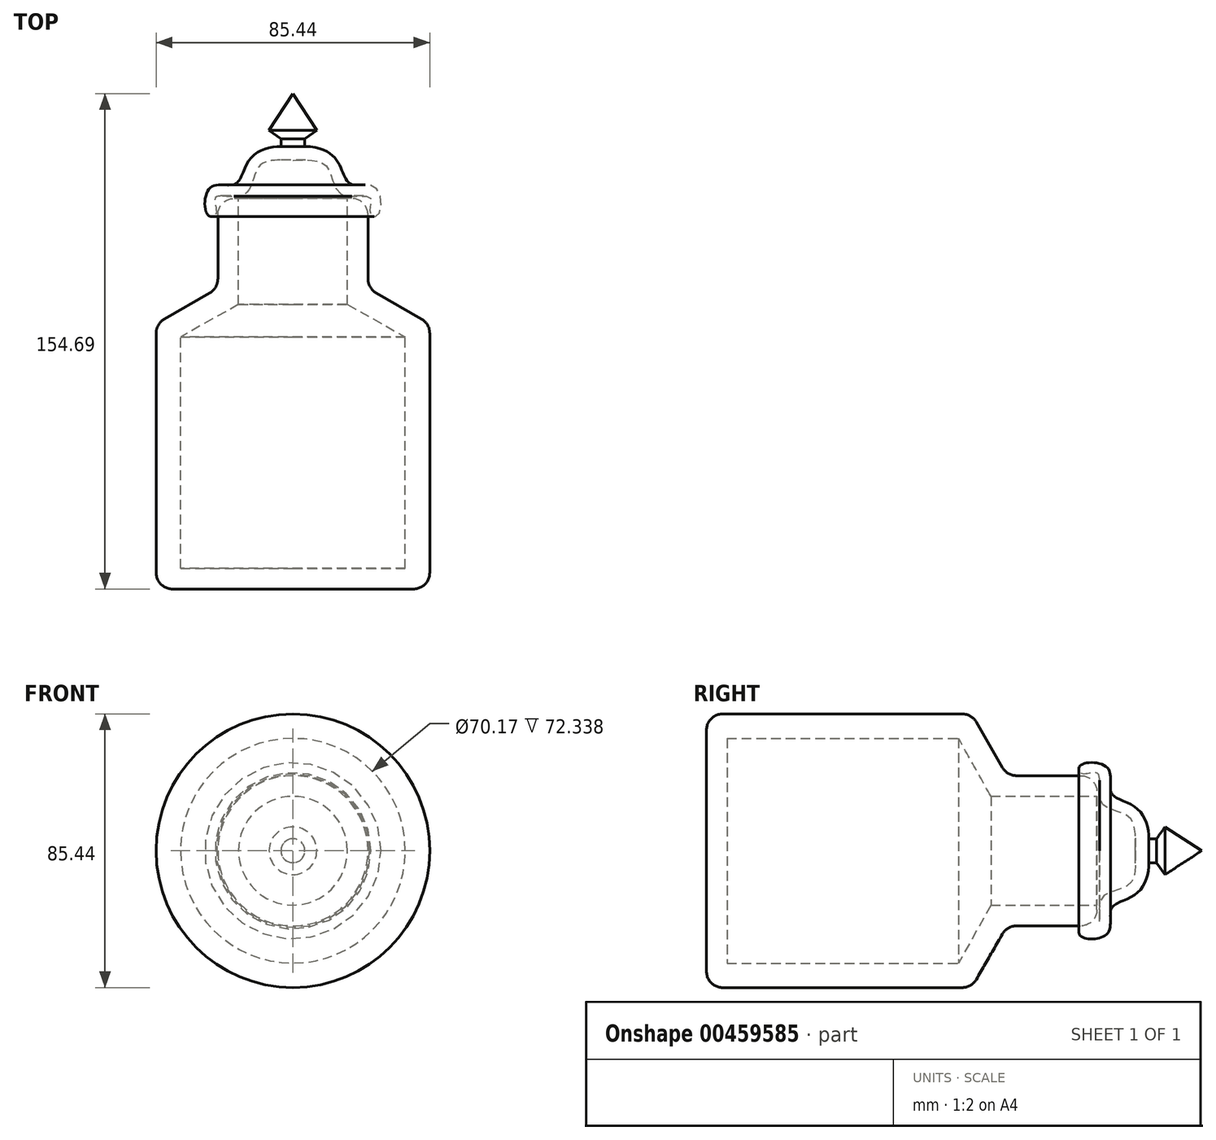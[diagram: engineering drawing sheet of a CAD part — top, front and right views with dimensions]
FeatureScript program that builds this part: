
annotation { "Feature Type Name" : "Feature", "Feature Type Description" : "" }
export const myFeature = defineFeature(function(context is Context, id is Id, definition is map)
    precondition{}
    {
        {
            var Q0;
            Q0=qCreatedBy(makeId("Top.planeOp"),FACE);
            var sketch = newSketch(context, id + "F0", { "sketchPlane" : qUnion([Q0])});
            skLineSegment(sketch, "E0", {"start": v(0, 75.39) * mm, "end": v(0, -75.47) * mm});
            skLineSegment(sketch, "E1", {"start": v(0, -64.48) * mm, "end": v(42.72, -64.48) * mm});
            skLineSegment(sketch, "E2", {"start": v(42.72, -64.48) * mm, "end": v(42.72, 18.34) * mm});
            skLineSegment(sketch, "E3", {"start": v(42.72, 18.34) * mm, "end": v(23.45, 29.44) * mm});
            skLineSegment(sketch, "E4", {"start": v(23.45, 29.44) * mm, "end": v(23.45, 57.48) * mm});
            skLineSegment(sketch, "E5", {"start": v(23.45, 57.48) * mm, "end": v(16.99, 57.48) * mm});
            skLineSegment(sketch, "E6", {"start": v(16.99, 57.48) * mm, "end": v(16.99, 24.36) * mm});
            skLineSegment(sketch, "E7", {"start": v(16.99, 24.36) * mm, "end": v(35.09, 14.27) * mm});
            skLineSegment(sketch, "E8", {"start": v(35.09, 14.27) * mm, "end": v(35.09, -58.07) * mm});
            skLineSegment(sketch, "E9", {"start": v(35.09, -58.07) * mm, "end": v(0, -58.07) * mm});
            skLineSegment(sketch, "E10", {"start": v(0, 75.39) * mm, "end": v(0, 95.93) * mm});
            skFitSpline(sketch, "E11", {"points": [v(0, 69.4) * mm, v(10.5, 67.6) * mm, v(15.16, 58.75) * mm, v(24.12, 57.75) * mm, v(24.06, 52.73) * mm, v(26.53, 52.26) * mm, v(25.73, 60.9) * mm, v(17.61, 62.26) * mm, v(3.72, 73.7) * mm], "startDerivative": vector(90.25, 0.02) * mm, "endDerivative": vector(-199.47, 2.25) * mm});
            skLineSegment(sketch, "E12", {"start": v(7.45, 78.77) * mm, "end": v(0, 90.21) * mm});
            skPoint(sketch, "E13.end.orphan", {"position": v(3.72, 78.77) * mm});
            skLineSegment(sketch, "E14", {"start": v(3.72, 73.7) * mm, "end": v(3.72, 76.1) * mm});
            skLineSegment(sketch, "E15", {"start": v(7.45, 78.77) * mm, "end": v(3.72, 76.1) * mm});
            skSolve(sketch);
        }
        {
            var Q0;
            Q0 = qSketchRegion(id + "F0", true);
            var Q1;
            Q1=sQuery(id+"F0.wireOp",EDGE,"E0");
            revolve(context, id + "F1", {"entities" : qUnion([Q0]), "axis" : qUnion([Q1]), "revolveType" : RevolveType.FULL});
        }
        {
            var Q0;
            Q0=makeQuery(id+"F1.opRevolve","SWEPT_EDGE",EDGE,{"disambiguationData":[OSD([sQuery(id+"F0.wireOp",EDGE,"E2"),sQuery(id+"F0.wireOp",EDGE,"E3")])]});
            var Q1;
            Q1=makeQuery(id+"F1.opRevolve","SWEPT_EDGE",EDGE,{"disambiguationData":[OSD([sQuery(id+"F0.wireOp",EDGE,"E4"),sQuery(id+"F0.wireOp",EDGE,"E5")])]});
            var Q2;
            Q2=makeQuery(id+"F1.opRevolve","SWEPT_EDGE",EDGE,{"disambiguationData":[OSD([sQuery(id+"F0.wireOp",EDGE,"E1"),sQuery(id+"F0.wireOp",EDGE,"E2")])]});
            var Q3;
            Q3=makeQuery(id+"F1.opRevolve","SWEPT_FACE",FACE,{"disambiguationData":[OSD([sQuery(id+"F0.wireOp",EDGE,"E2")])]});
            var Q4;
            Q4=makeQuery(id+"F1.opRevolve","SWEPT_FACE",FACE,{"disambiguationData":[OSD([sQuery(id+"F0.wireOp",EDGE,"E3")])]});
            var Q5;
            Q5=makeQuery(id+"F1.opRevolve","SWEPT_FACE",FACE,{"disambiguationData":[OSD([sQuery(id+"F0.wireOp",EDGE,"E4")])]});
            fillet(context, id + "F2", {"entities" : qUnion([Q0, Q1, Q2, Q3, Q4, Q5]), "radius" : 5.08 * mm, "tangentPropagation" : true, "allowEdgeOverflow" : false});
        }
    });
